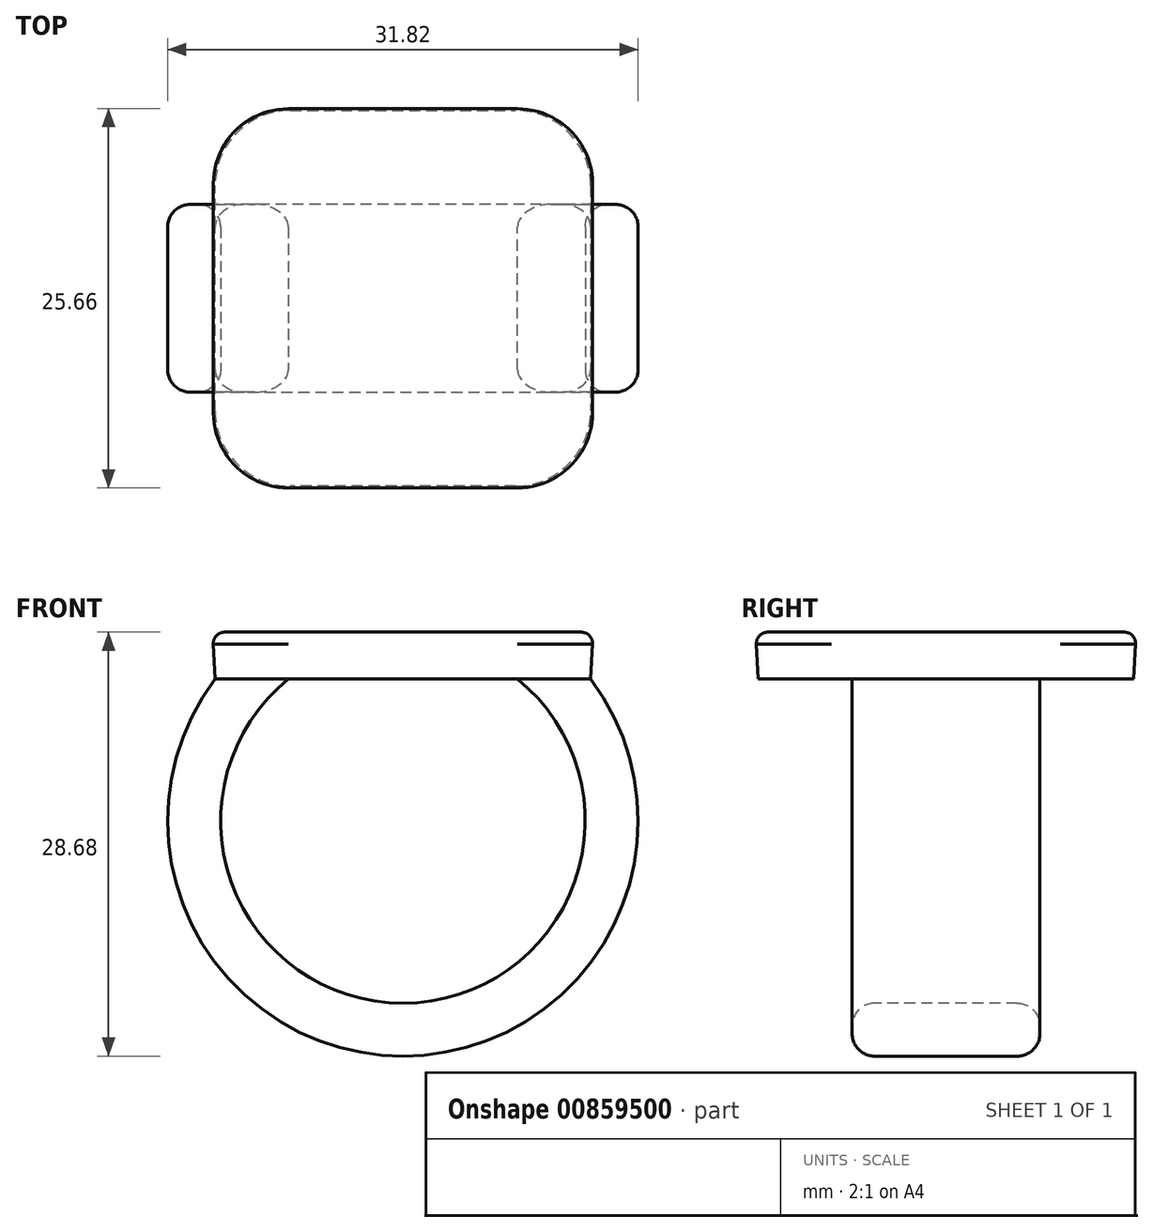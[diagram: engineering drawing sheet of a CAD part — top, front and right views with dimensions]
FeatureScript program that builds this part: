
annotation { "Feature Type Name" : "Feature", "Feature Type Description" : "" }
export const myFeature = defineFeature(function(context is Context, id is Id, definition is map)
    precondition{}
    {
        {
            var Q0;
            Q0=qCreatedBy(makeId("Top.planeOp"),FACE);
            var sketch = newSketch(context, id + "F0", { "sketchPlane" : qUnion([Q0])});
            skLineSegment(sketch, "E0.bottom", {"start": v(12.7, -12.7) * mm, "end": v(-12.7, -12.7) * mm});
            skLineSegment(sketch, "E0.top", {"start": v(12.7, 12.7) * mm, "end": v(-12.7, 12.7) * mm});
            skLineSegment(sketch, "E0.left", {"start": v(12.7, -12.7) * mm, "end": v(12.7, 12.7) * mm});
            skLineSegment(sketch, "E0.right", {"start": v(-12.7, -12.7) * mm, "end": v(-12.7, 12.7) * mm});
            skPoint(sketch, "E0.middle", {"position": v(0, 0) * mm});
            skSolve(sketch);
        }
        {
            var Q0;
            Q0=makeQuery(id+"F0.imprint","IMPRINT",FACE,{"disambiguationData":[TD([[makeQuery(id+"F0.imprint","IMPRINT",EDGE,{"derivedFrom":sQuery(id+"F0.wireOp",EDGE,"E0.bottom")}),-1.0]])]});
            extrude(context, id + "F1", {"entities" : qUnion([Q0]), "depth" : 3.17 * mm, "offsetDistance" : 25.4 * mm, "hasDraft" : true, "draftAngle" : 3 * degree});
        }
        {
            var Q0;
            Q0=qCreatedBy(makeId("Front.planeOp"),FACE);
            var sketch = newSketch(context, id + "F2", { "sketchPlane" : qUnion([Q0])});
            skArc(sketch, "E1", {"start": v(-10.16, 0) * mm, "mid": v(0, -23.56) * mm, "end": v(10.16, 0) * mm});
            skSolve(sketch);
        }
        {
            var Q0;
            Q0=makeQuery(id+"F1.opExtrude","CAP_FACE",FACE,{"disambiguationData":[OSD([sQuery(id+"F0.wireOp",EDGE,"E0.bottom"),sQuery(id+"F0.wireOp",EDGE,"E0.top"),sQuery(id+"F0.wireOp",EDGE,"E0.left"),sQuery(id+"F0.wireOp",EDGE,"E0.right")])],"isStart":true});
            var sketch = newSketch(context, id + "F3", { "sketchPlane" : qUnion([Q0])});
            skLineSegment(sketch, "E2.bottom", {"start": v(-7.75, -6.35) * mm, "end": v(-12.83, -6.35) * mm});
            skLineSegment(sketch, "E2.top", {"start": v(-7.75, 6.35) * mm, "end": v(-12.83, 6.35) * mm});
            skLineSegment(sketch, "E2.left", {"start": v(-7.75, -6.35) * mm, "end": v(-7.75, 6.35) * mm});
            skLineSegment(sketch, "E2.right", {"start": v(-12.83, -6.35) * mm, "end": v(-12.83, 6.35) * mm});
            skPoint(sketch, "E2.middle", {"position": v(-10.3, 0) * mm});
            skSolve(sketch);
        }
        {
            var Q0;
            {var subQ0=sQuery(id+"F3.wireOp",EDGE,"E2.left");Q0=makeQuery(id+"F3.imprint","IMPRINT",FACE,{"disambiguationData":[TD([[makeQuery(id+"F3.imprint","IMPRINT",EDGE,{"derivedFrom":subQ0}),1.0]])]});}
            var Q1;
            Q1=sQuery(id+"F2.wireOp",EDGE,"E1");
            sweep(context, id + "F4", {"operationType" : NewBodyOperationType.ADD, "profiles" : qUnion([Q0]), "path" : qUnion([Q1])});
        }
        {
            var Q0;
            Q0=qCreatedBy(makeId("Front.planeOp"),FACE);
            var sketch = newSketch(context, id + "F5", { "sketchPlane" : qUnion([Q0])});
            skLineSegment(sketch, "E3.0", {"start": v(10.16, 0) * mm, "end": v(7.75, 0) * mm});
            skArc(sketch, "E3.1", {"start": v(10.02, -2.4) * mm, "mid": v(8.97, -1.13) * mm, "end": v(7.75, 0) * mm});
            skLineSegment(sketch, "E3.2", {"start": v(10.02, -2.4) * mm, "end": v(10.16, 0) * mm});
            skPoint(sketch, "E4.orphan", {"position": v(-7.75, 0) * mm});
            skPoint(sketch, "E5.orphan", {"position": v(12.7, 0) * mm});
            skPoint(sketch, "E6.trimOffspring.end.orphan", {"position": v(-12.7, 0) * mm});
            skSolve(sketch);
        }
        {
            var Q0;
            Q0=makeQuery(id+"F5.imprint","IMPRINT",FACE,{"disambiguationData":[TD([[makeQuery(id+"F5.imprint","IMPRINT",EDGE,{"derivedFrom":sQuery(id+"F5.wireOp",EDGE,"E3.0")}),1.0]])]});
            var Q1;
            Q1=makeQuery(id+"F4.opSweep","SWEPT_FACE",FACE,{"disambiguationData":[OSD([sQuery(id+"F2.wireOp",EDGE,"E1"),sQuery(id+"F3.wireOp",EDGE,"E2.top")])]});
            var Q2;
            Q2=makeQuery(id+"F4.opSweep","SWEPT_FACE",FACE,{"disambiguationData":[OSD([sQuery(id+"F2.wireOp",EDGE,"E1"),sQuery(id+"F3.wireOp",EDGE,"E2.bottom")])]});
            extrude(context, id + "F6", {"entities" : qUnion([Q0]), "operationType" : NewBodyOperationType.ADD, "endBound" : BoundingType.UP_TO_SURFACE, "depth" : 25.4 * mm, "endBoundEntityFace" : qUnion([Q1]), "offsetDistance" : 25.4 * mm, "hasSecondDirection" : true, "secondDirectionBound" : SecondDirectionBoundingType.UP_TO_SURFACE, "secondDirectionOppositeDirection" : true, "secondDirectionDepth" : 25.4 * mm, "secondDirectionBoundEntityFace" : qUnion([Q2])});
        }
        {
            var Q0;
            Q0=makeQuery(id+"F1.opExtrude","SWEPT_EDGE",EDGE,{"disambiguationData":[OSD([sQuery(id+"F0.wireOp",EDGE,"E0.bottom"),sQuery(id+"F0.wireOp",EDGE,"E0.right")])]});
            var Q1;
            Q1=makeQuery(id+"F1.opExtrude","SWEPT_EDGE",EDGE,{"disambiguationData":[OSD([sQuery(id+"F0.wireOp",EDGE,"E0.bottom"),sQuery(id+"F0.wireOp",EDGE,"E0.left")])]});
            var Q2;
            Q2=makeQuery(id+"F1.opExtrude","SWEPT_EDGE",EDGE,{"disambiguationData":[OSD([sQuery(id+"F0.wireOp",EDGE,"E0.top"),sQuery(id+"F0.wireOp",EDGE,"E0.left")])]});
            var Q3;
            Q3=makeQuery(id+"F1.opExtrude","SWEPT_EDGE",EDGE,{"disambiguationData":[OSD([sQuery(id+"F0.wireOp",EDGE,"E0.top"),sQuery(id+"F0.wireOp",EDGE,"E0.right")])]});
            fillet(context, id + "F7", {"entities" : qUnion([Q0, Q1, Q2, Q3]), "radius" : 5.08 * mm, "tangentPropagation" : true, "allowEdgeOverflow" : false});
        }
        {
            var Q0;
            Q0=makeQuery(id+"F4.opSweep","SWEPT_EDGE",EDGE,{"disambiguationData":[OSD([sQuery(id+"F0.wireOp",EDGE,"E0.right"),sQuery(id+"F2.wireOp",EDGE,"E1"),sQuery(id+"F3.wireOp",EDGE,"E2.top")])]});
            var Q1;
            Q1=makeQuery(id+"F6.boolean.opBoolean","MERGE",EDGE,{"derivedFrom":[makeQuery(id+"F4.opSweep","SWEPT_EDGE",EDGE,{"disambiguationData":[OSD([sQuery(id+"F2.wireOp",EDGE,"E1"),sQuery(id+"F3.wireOp",EDGE,"E2.top"),sQuery(id+"F3.wireOp",EDGE,"E2.left")])]}),makeQuery(id+"F6.opExtrude","CAP_EDGE",EDGE,{"disambiguationData":[OSD([sQuery(id+"F5.wireOp",EDGE,"E3.1")])],"isStart":false})]});
            var Q2;
            Q2=makeQuery(id+"F4.opSweep","SWEPT_EDGE",EDGE,{"disambiguationData":[OSD([sQuery(id+"F0.wireOp",EDGE,"E0.right"),sQuery(id+"F2.wireOp",EDGE,"E1"),sQuery(id+"F3.wireOp",EDGE,"E2.bottom")])]});
            var Q3;
            Q3=makeQuery(id+"F6.boolean.opBoolean","MERGE",EDGE,{"derivedFrom":[makeQuery(id+"F4.opSweep","SWEPT_EDGE",EDGE,{"disambiguationData":[OSD([sQuery(id+"F2.wireOp",EDGE,"E1"),sQuery(id+"F3.wireOp",EDGE,"E2.bottom"),sQuery(id+"F3.wireOp",EDGE,"E2.left")])]}),makeQuery(id+"F6.opExtrude","CAP_EDGE",EDGE,{"disambiguationData":[OSD([sQuery(id+"F5.wireOp",EDGE,"E3.1")])],"isStart":true})]});
            fillet(context, id + "F8", {"entities" : qUnion([Q0, Q1, Q2, Q3]), "radius" : 1.52 * mm, "tangentPropagation" : true, "allowEdgeOverflow" : false});
        }
        {
            var Q0;
            Q0=makeQuery(id+"F1.opExtrude","CAP_FACE",FACE,{"disambiguationData":[OSD([sQuery(id+"F0.wireOp",EDGE,"E0.bottom"),sQuery(id+"F0.wireOp",EDGE,"E0.top"),sQuery(id+"F0.wireOp",EDGE,"E0.left"),sQuery(id+"F0.wireOp",EDGE,"E0.right")])],"isStart":false});
            fillet(context, id + "F9", {"entities" : qUnion([Q0]), "radius" : 0.76 * mm, "tangentPropagation" : true, "allowEdgeOverflow" : false});
        }
    });
